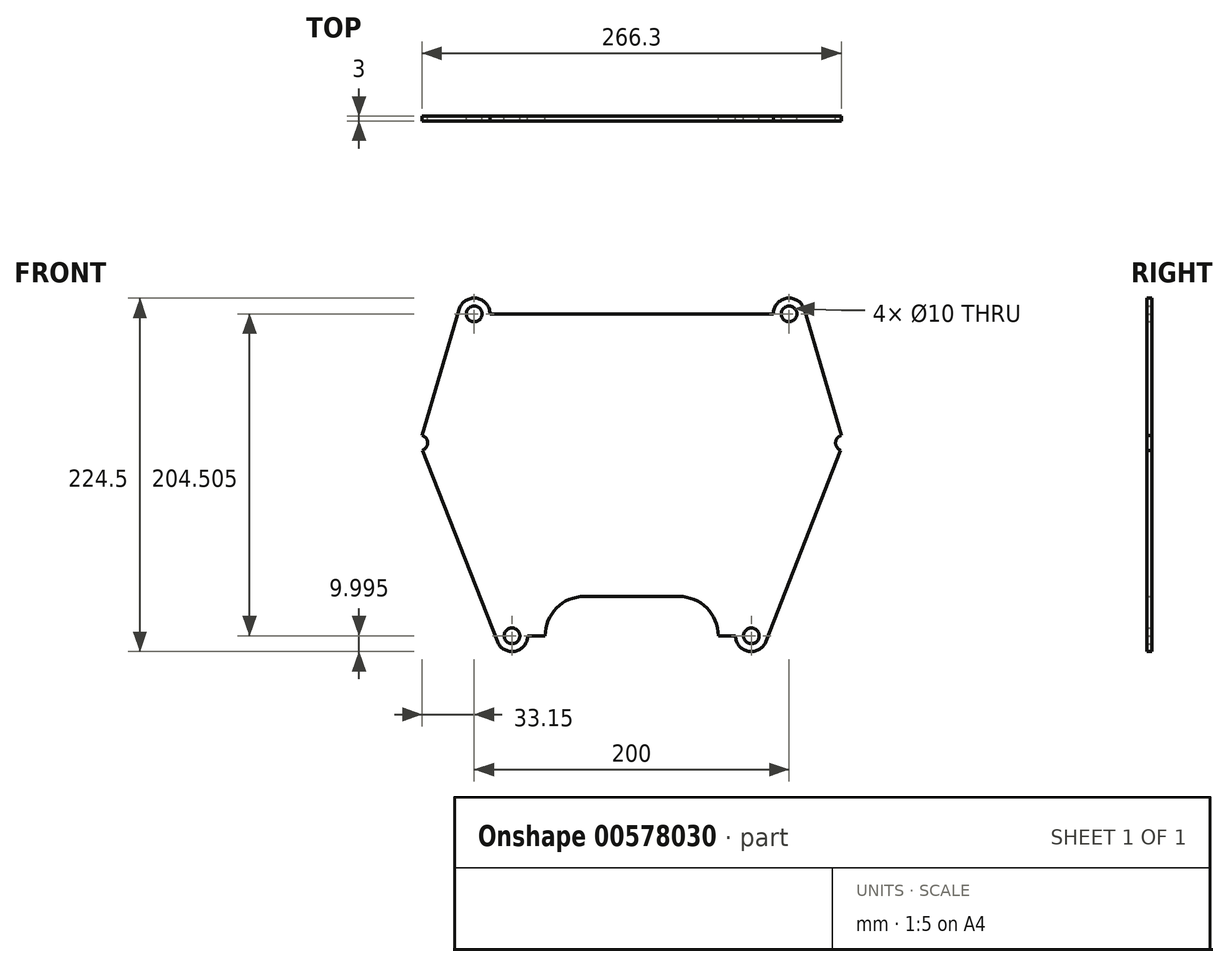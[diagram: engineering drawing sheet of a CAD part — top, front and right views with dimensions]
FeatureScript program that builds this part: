
annotation { "Feature Type Name" : "Feature", "Feature Type Description" : "" }
export const myFeature = defineFeature(function(context is Context, id is Id, definition is map)
    precondition{}
    {
        {
            var Q0;
            Q0=qCreatedBy(makeId("Front.planeOp"),FACE);
            var sketch = newSketch(context, id + "F0", { "sketchPlane" : qUnion([Q0])});
            skLineSegment(sketch, "E0", {"start": v(-100, 0) * mm, "end": v(-190, 0) * mm});
            skLineSegment(sketch, "E1", {"start": v(-100, 0) * mm, "end": v(-100, -204.5) * mm, "construction": true});
            skLineSegment(sketch, "E2", {"start": v(-100, -81.54) * mm, "end": v(-224, -81.54) * mm, "construction": true});
            skCircle(sketch, "E3", {"center": v(-200, 0) * mm, "radius": 5 * mm});
            skCircle(sketch, "E4", {"center": v(-176, -204.5) * mm, "radius": 5 * mm});
            skLineSegment(sketch, "E5.0", {"start": v(-209.6, 2.82) * mm, "end": v(-233.15, -77.2) * mm});
            skArc(sketch, "E6", {"start": v(-190, 0) * mm, "mid": v(-198.57, 9.9) * mm, "end": v(-209.6, 2.82) * mm});
            skLineSegment(sketch, "E7.0", {"start": v(-232.74, -86.65) * mm, "end": v(-185.32, -208.14) * mm});
            skArc(sketch, "E8", {"start": v(-185.32, -208.14) * mm, "mid": v(-174.15, -214.33) * mm, "end": v(-166, -204.5) * mm});
            skLineSegment(sketch, "E9.0", {"start": v(-100, -179.5) * mm, "end": v(-130, -179.5) * mm});
            skArc(sketch, "E10", {"start": v(-130, -179.5) * mm, "mid": v(-147.68, -186.83) * mm, "end": v(-155, -204.5) * mm});
            skLineSegment(sketch, "E11.trimOffspring", {"start": v(-155, -204.5) * mm, "end": v(-166, -204.5) * mm});
            skArc(sketch, "E12", {"start": v(-232.74, -86.65) * mm, "mid": v(-229.56, -81.78) * mm, "end": v(-233.15, -77.2) * mm});
            skPoint(sketch, "E13.orphan", {"position": v(0, 0) * mm});
            skPoint(sketch, "E14.MirrorCS.end.orphan", {"position": v(24, -81.54) * mm});
            skPoint(sketch, "E15.MirrorCS.end.orphan", {"position": v(-24, -204.5) * mm});
            skPoint(sketch, "E16.MirrorCS.start.orphan", {"position": v(-100, -204.5) * mm});
            skLineSegment(sketch, "E17.MirrorCS", {"start": v(-100, 0) * mm, "end": v(-10, 0) * mm});
            skArc(sketch, "E18.MirrorCS", {"start": v(-10, 0) * mm, "mid": v(-1.43, 9.9) * mm, "end": v(9.6, 2.82) * mm});
            skLineSegment(sketch, "E19.MirrorCS", {"start": v(9.6, 2.82) * mm, "end": v(33.15, -77.2) * mm});
            skCircle(sketch, "E20.MirrorC", {"center": v(0, 0) * mm, "radius": 5 * mm});
            skArc(sketch, "E21.MirrorCS", {"start": v(32.74, -86.65) * mm, "mid": v(29.56, -81.78) * mm, "end": v(33.15, -77.2) * mm});
            skLineSegment(sketch, "E22.MirrorCS", {"start": v(32.74, -86.65) * mm, "end": v(-14.68, -208.14) * mm});
            skArc(sketch, "E23.MirrorCS", {"start": v(-14.68, -208.14) * mm, "mid": v(-25.85, -214.33) * mm, "end": v(-34, -204.5) * mm});
            skCircle(sketch, "E24.MirrorC", {"center": v(-24, -204.5) * mm, "radius": 5 * mm});
            skLineSegment(sketch, "E25.MirrorCS", {"start": v(-45, -204.5) * mm, "end": v(-34, -204.5) * mm});
            skArc(sketch, "E26.MirrorCS", {"start": v(-70, -179.5) * mm, "mid": v(-52.32, -186.83) * mm, "end": v(-45, -204.5) * mm});
            skLineSegment(sketch, "E27.MirrorCS", {"start": v(-100, -179.5) * mm, "end": v(-70, -179.5) * mm});
            skSolve(sketch);
        }
        {
            var Q0;
            Q0=makeQuery(id+"F0.imprint","IMPRINT",FACE,{"disambiguationData":[TD([[makeQuery(id+"F0.imprint","IMPRINT",EDGE,{"derivedFrom":sQuery(id+"F0.wireOp",EDGE,"E0")}),1.0]])]});
            extrude(context, id + "F1", {"entities" : qUnion([Q0]), "depth" : 3 * mm, "offsetDistance" : 25 * mm});
        }
    });
